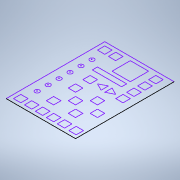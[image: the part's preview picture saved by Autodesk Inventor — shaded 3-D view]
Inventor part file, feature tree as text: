
AUTODESK INVENTOR PART (.ipt)
format: ipt  version: 2021.1 (Build 251245000, 245)  size: 113,152 bytes
history: native  units: mm
features: sketch x1
ambient origin geometry x8: Origin, YZ Plane, XZ Plane, XY Plane, X Axis, Y Axis, Z Axis, Center Point
feature tree (1):
  sketch  "Sketch1"
